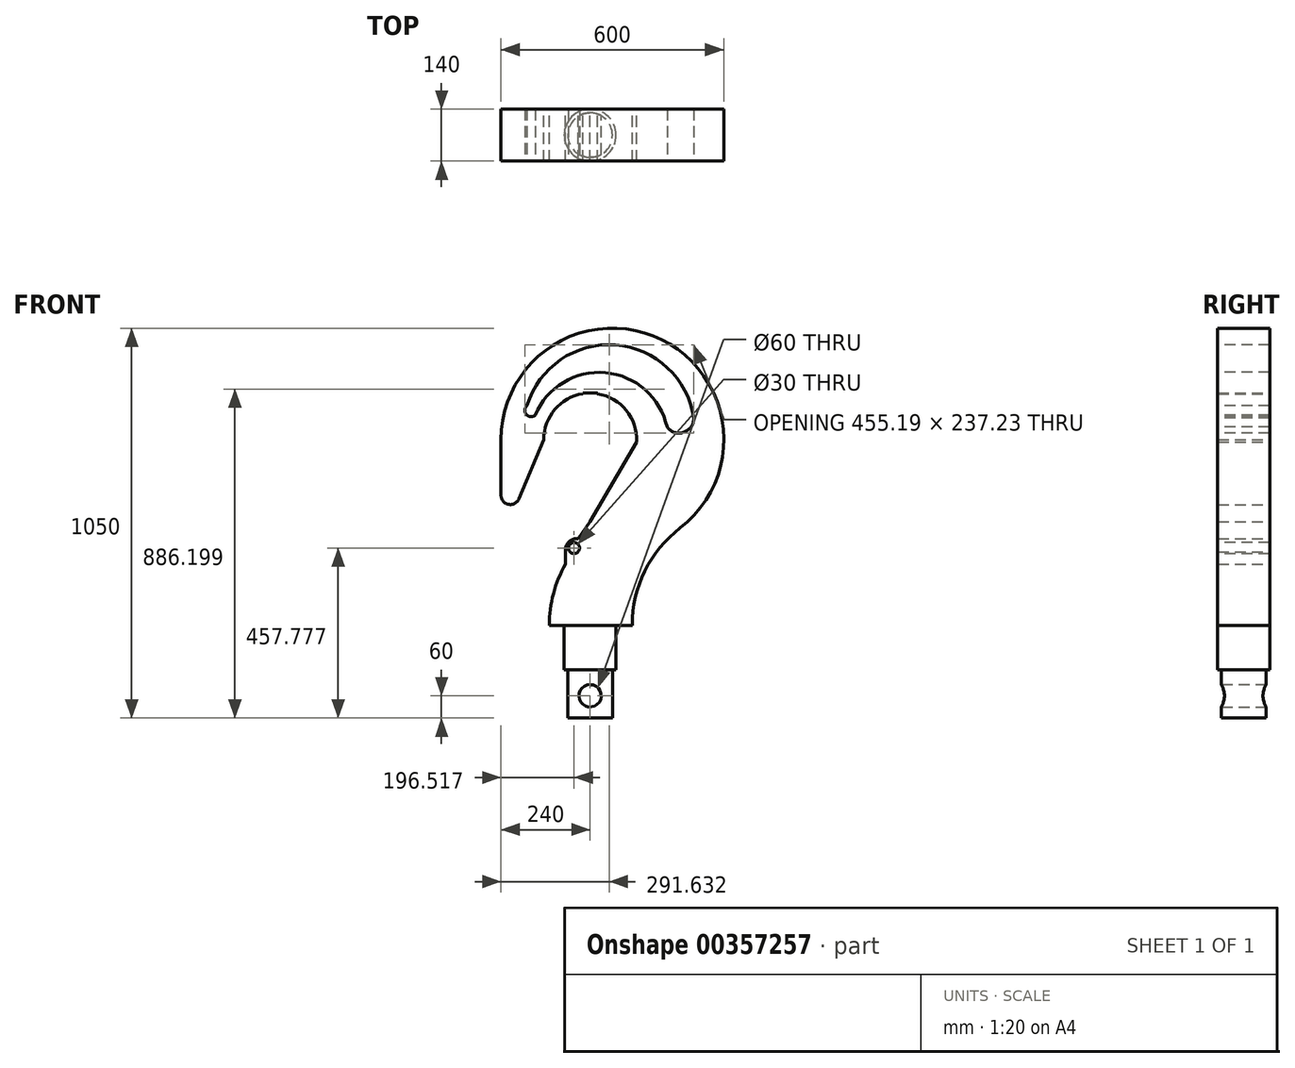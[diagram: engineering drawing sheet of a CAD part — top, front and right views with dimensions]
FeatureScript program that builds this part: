
annotation { "Feature Type Name" : "Feature", "Feature Type Description" : "" }
export const myFeature = defineFeature(function(context is Context, id is Id, definition is map)
    precondition{}
    {
        {
            var Q0;
            Q0=qCreatedBy(makeId("Front.planeOp"),FACE);
            var sketch = newSketch(context, id + "F0", { "sketchPlane" : qUnion([Q0])});
            skArc(sketch, "E0", {"start": v(242.51, 261.9) * mm, "mid": v(147.34, 146.03) * mm, "end": v(113.28, 0) * mm});
            skArc(sketch, "E1", {"start": v(-66.06, 164.53) * mm, "mid": v(-98.83, 85.15) * mm, "end": v(-110, 0) * mm});
            skLineSegment(sketch, "E2", {"start": v(0, 898.51) * mm, "end": v(0, -968.16) * mm, "construction": true});
            skArc(sketch, "E3", {"start": v(124.84, 493.61) * mm, "mid": v(97.24, 578.55) * mm, "end": v(20, 623.39) * mm});
            skArc(sketch, "E4", {"start": v(242.51, 261.9) * mm, "mid": v(192.75, 769.03) * mm, "end": v(-240, 500) * mm});
            skLineSegment(sketch, "E5", {"start": v(124.84, 493.61) * mm, "end": v(0, 278.41) * mm});
            skLineSegment(sketch, "E6", {"start": v(-607.5, 0) * mm, "end": v(1252.05, 0) * mm, "construction": true});
            skLineSegment(sketch, "E7", {"start": v(0, 500) * mm, "end": v(-349.97, 500) * mm, "construction": true});
            skLineSegment(sketch, "E8", {"start": v(-240, 500) * mm, "end": v(-125, 500) * mm});
            skArc(sketch, "E9", {"start": v(-240, 350) * mm, "mid": v(-219.93, 325.5) * mm, "end": v(-191.94, 340.33) * mm});
            skLineSegment(sketch, "E10", {"start": v(-240, 500) * mm, "end": v(-240, 350) * mm});
            skLineSegment(sketch, "E11", {"start": v(-125, 500) * mm, "end": v(-191.94, 340.33) * mm});
            skLineSegment(sketch, "E12", {"start": v(-110, 0) * mm, "end": v(113.28, 0) * mm});
            skPoint(sketch, "E13.oppositeSnap0", {"position": v(20, 623.39) * mm});
            skLineSegment(sketch, "E13.top", {"start": v(-20, 624.95) * mm, "end": v(20, 624.95) * mm});
            skLineSegment(sketch, "E13.left", {"start": v(-20, 623.39) * mm, "end": v(-20, 624.95) * mm});
            skLineSegment(sketch, "E13.right", {"start": v(20, 623.39) * mm, "end": v(20, 624.95) * mm});
            skArc(sketch, "E14.trimOffspring", {"start": v(-20, 623.39) * mm, "mid": v(-95.2, 581) * mm, "end": v(-125, 500) * mm});
            skLineSegment(sketch, "E15.trimOffspring", {"start": v(55.5, 612) * mm, "end": v(68.67, 612) * mm, "construction": true});
            skLineSegment(sketch, "E16", {"start": v(-66.06, 164.53) * mm, "end": v(-66.06, 197.07) * mm});
            skArc(sketch, "E17", {"start": v(-31.67, 232.57) * mm, "mid": v(-58.2, 223.86) * mm, "end": v(-66.06, 197.07) * mm});
            skLineSegment(sketch, "E18", {"start": v(-31.67, 232.57) * mm, "end": v(0, 278.41) * mm});
            skSolve(sketch);
        }
        {
            var Q0;
            Q0=qCreatedBy(makeId("Front.planeOp"),FACE);
            var sketch = newSketch(context, id + "F1", { "sketchPlane" : qUnion([Q0])});
            skLineSegment(sketch, "E19", {"start": v(-60, -250) * mm, "end": v(0, -250) * mm});
            skLineSegment(sketch, "E20", {"start": v(-70, 0) * mm, "end": v(0, 0) * mm});
            skLineSegment(sketch, "E21", {"start": v(0, 0) * mm, "end": v(0, -250) * mm});
            skLineSegment(sketch, "E22", {"start": v(-70, -120) * mm, "end": v(-70, 0) * mm});
            skLineSegment(sketch, "E23", {"start": v(-70, -120) * mm, "end": v(-60, -120) * mm});
            skLineSegment(sketch, "E24", {"start": v(-60, -120) * mm, "end": v(-60, -250) * mm});
            skSolve(sketch);
        }
        {
            var Q0;
            Q0=qSketchRegion(id+"F1",true);
            var Q1;
            Q1=sQuery(id+"F1.wireOp",EDGE,"E21");
            revolve(context, id + "F2", {"entities" : qUnion([Q0]), "axis" : qUnion([Q1]), "revolveType" : RevolveType.FULL});
        }
        {
            var Q0;
            Q0=makeQuery(id+"F0.imprint","IMPRINT",FACE,{"disambiguationData":[TD([[makeQuery(id+"F0.imprint","IMPRINT",EDGE,{"derivedFrom":sQuery(id+"F0.wireOp",EDGE,"E0")}),-1.0]])]});
            var Q1;
            Q1=makeQuery(id+"F0.imprint","IMPRINT",FACE,{"disambiguationData":[TD([[makeQuery(id+"F0.imprint","IMPRINT",EDGE,{"derivedFrom":sQuery(id+"F0.wireOp",EDGE,"E8")}),-1.0]])]});
            extrude(context, id + "F3", {"entities" : qUnion([Q0, Q1]), "operationType" : NewBodyOperationType.ADD, "endBound" : BoundingType.SYMMETRIC, "depth" : 140 * mm});
        }
        {
            var Q0;
            Q0=qCreatedBy(makeId("Front.planeOp"),FACE);
            var sketch = newSketch(context, id + "F4", { "sketchPlane" : qUnion([Q0])});
            skCircle(sketch, "E25", {"center": v(0, -190) * mm, "radius": 30 * mm});
            skSolve(sketch);
        }
        {
            var Q0;
            Q0=qSketchRegion(id+"F4",true);
            extrude(context, id + "F5", {"entities" : qUnion([Q0]), "operationType" : NewBodyOperationType.REMOVE, "endBound" : BoundingType.SYMMETRIC, "depth" : 224 * mm});
        }
        {
            var Q0;
            Q0=makeQuery(id+"F3.opExtrude","CAP_FACE",FACE,{"disambiguationData":[OSD([sQuery(id+"F0.wireOp",EDGE,"E0"),sQuery(id+"F0.wireOp",EDGE,"E1"),sQuery(id+"F0.wireOp",EDGE,"E3"),sQuery(id+"F0.wireOp",EDGE,"E4"),sQuery(id+"F0.wireOp",EDGE,"E5"),sQuery(id+"F0.wireOp",EDGE,"E9"),sQuery(id+"F0.wireOp",EDGE,"E10"),sQuery(id+"F0.wireOp",EDGE,"E11"),sQuery(id+"F0.wireOp",EDGE,"E12"),sQuery(id+"F0.wireOp",EDGE,"E13.top"),sQuery(id+"F0.wireOp",EDGE,"E13.left"),sQuery(id+"F0.wireOp",EDGE,"E13.right"),sQuery(id+"F0.wireOp",EDGE,"E14.trimOffspring")])],"isStart":false});
            var sketch = newSketch(context, id + "F6", { "sketchPlane" : qUnion([Q0])});
            skCircle(sketch, "E26", {"center": v(-43.48, 207.78) * mm, "radius": 15 * mm});
            skSolve(sketch);
        }
        {
            var Q0;
            Q0=qSketchRegion(id+"F6",true);
            var Q1;
            Q1=makeQuery(id+"F6.imprint","IMPRINT",FACE,{"disambiguationData":[TD([[makeQuery(id+"F6.imprint","IMPRINT",EDGE,{"derivedFrom":sQuery(id+"F6.wireOp",EDGE,"E26")}),1.0]])]});
            extrude(context, id + "F7", {"entities" : qUnion([Q0, Q1]), "operationType" : NewBodyOperationType.REMOVE, "endBound" : BoundingType.SYMMETRIC, "oppositeDirection" : true, "depth" : 326 * mm});
        }
        {
            var Q0;
            Q0=makeQuery(id+"F3.opExtrude","CAP_FACE",FACE,{"disambiguationData":[OSD([sQuery(id+"F0.wireOp",EDGE,"E0"),sQuery(id+"F0.wireOp",EDGE,"E1"),sQuery(id+"F0.wireOp",EDGE,"E3"),sQuery(id+"F0.wireOp",EDGE,"E4"),sQuery(id+"F0.wireOp",EDGE,"E5"),sQuery(id+"F0.wireOp",EDGE,"E9"),sQuery(id+"F0.wireOp",EDGE,"E10"),sQuery(id+"F0.wireOp",EDGE,"E11"),sQuery(id+"F0.wireOp",EDGE,"E12"),sQuery(id+"F0.wireOp",EDGE,"E13.top"),sQuery(id+"F0.wireOp",EDGE,"E13.left"),sQuery(id+"F0.wireOp",EDGE,"E13.right"),sQuery(id+"F0.wireOp",EDGE,"E14.trimOffspring"),sQuery(id+"F0.wireOp",EDGE,"E16"),sQuery(id+"F0.wireOp",EDGE,"E17"),sQuery(id+"F0.wireOp",EDGE,"E18")])],"isStart":false});
            var sketch = newSketch(context, id + "F8", { "sketchPlane" : qUnion([Q0])});
            skArc(sketch, "E27", {"start": v(279.23, 557.56) * mm, "mid": v(68.17, 754.81) * mm, "end": v(-170.1, 591.46) * mm});
            skArc(sketch, "E28", {"start": v(207.24, 533.56) * mm, "mid": v(41.28, 680) * mm, "end": v(-148.13, 565.5) * mm});
            skArc(sketch, "E29", {"start": v(-170.1, 591.46) * mm, "mid": v(-172, 567.58) * mm, "end": v(-148.13, 565.5) * mm});
            skArc(sketch, "E30", {"start": v(207.24, 533.56) * mm, "mid": v(251.88, 519.64) * mm, "end": v(279.23, 557.56) * mm});
            skSolve(sketch);
        }
        {
            var Q0;
            Q0 = qSketchRegion(id + "F8", true);
            var Q1;
            Q1=makeQuery(id+"F8.imprint","IMPRINT",FACE,{"disambiguationData":[TD([[makeQuery(id+"F8.imprint","IMPRINT",EDGE,{"derivedFrom":sQuery(id+"F8.wireOp",EDGE,"E27")}),1.0]])]});
            extrude(context, id + "F9", {"entities" : qUnion([Q0, Q1]), "operationType" : NewBodyOperationType.REMOVE, "oppositeDirection" : true, "depth" : 150 * mm});
        }
    });
